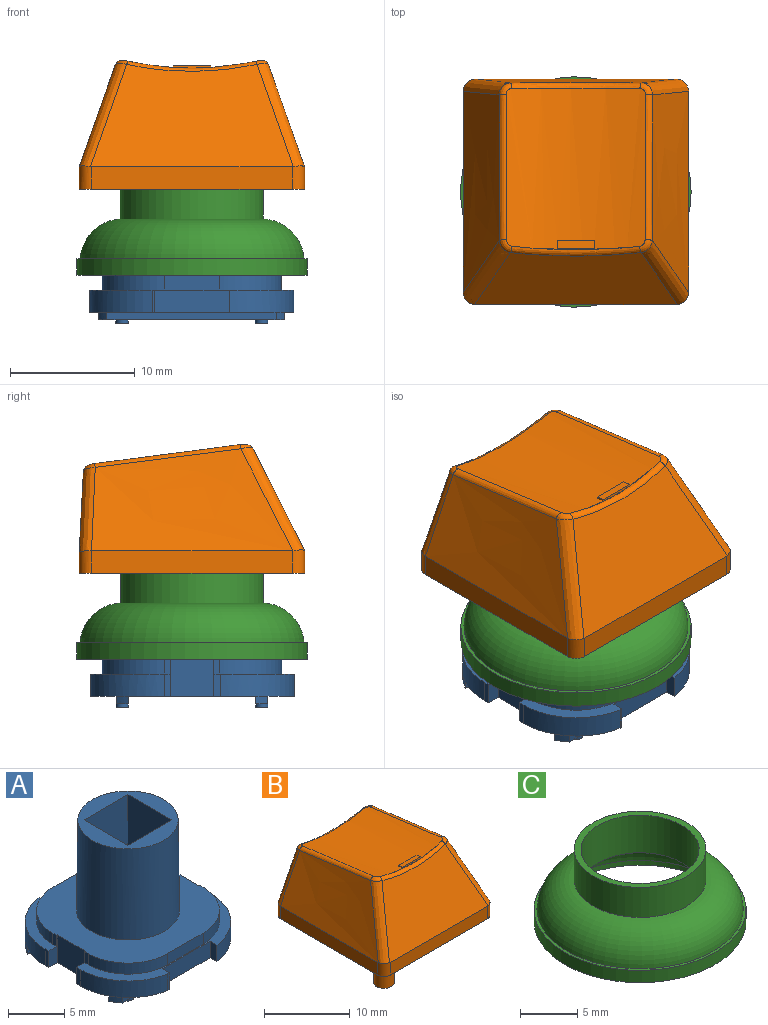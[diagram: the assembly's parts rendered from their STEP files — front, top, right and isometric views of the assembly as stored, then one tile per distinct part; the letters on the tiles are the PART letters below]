
ASSEMBLY  parts=3 mates=2
PART A: 86 faces, bbox 16.4x16.4x13.7 mm
  f0: plane 6x1.8mm, normal (0,1,0), area 10.8mm2, adj f3,f10,f11,f12
  f1: plane 1x1mm, normal (0,0,-1), area 0.8mm2, adj f13
  f2: plane 1x1mm, normal (0,0,-1), area 0.8mm2, adj f14
  f3: plane 1.8x0.85mm, normal (1,0,0), area 1.5mm2, adj f0,f11,f12,f26
  f4: plane 1.2x0.45mm, normal (-1,0,0), area 0.5mm2, adj f5,f11,f27,f28
  f5: revolved ~5x5mm, area 9.4mm2, adj f4,f6,f11,f28
  f6: plane 4.4x1.2mm, normal (0,1,0), area 5.3mm2, adj f5,f7,f11,f28
  f7: revolved ~5x5mm, area 9.4mm2, adj f6,f9,f11,f28
  f8: revolved ~9.8x9.13mm, area 277.6mm2, adj f19,f28
  f9: plane 1.2x0.45mm, normal (1,0,0), area 0.5mm2, adj f7,f11,f28,f29
  f10: plane 1.8x0.85mm, normal (-1,0,0), area 1.5mm2, adj f0,f11,f12,f31
  f11: plane 16.4x6.4mm, normal (0,0,1), area 17.2mm2, adj f0,f3,f4,f5,f6,f7,f9,f10
  f12: plane 13.52x2.05mm, normal (0,0,-1), area 17.2mm2, adj f0,f3,f10,f15,f26,f31
  f13: revolved ~1x1mm, area 0.9mm2, adj f1,f32,f33
  f14: revolved ~1x1mm, area 0.9mm2, adj f2,f33,f34
  f15: plane 13.52x0.6mm, normal (0,1,0), area 8.1mm2, adj f12,f32,f33,f34,f35,f36
  f16: plane 2.8x0.75mm, normal (0,0,-1), area 2.1mm2, adj f40,f41,f42,f43
  f17: plane 2.8x0.75mm, normal (0,0,-1), area 2.1mm2, adj f44,f45,f46,f47
  f18: plane 2.8x0.75mm, normal (0,0,-1), area 2.1mm2, adj f48,f49,f50,f51
  f19: plane 8.9x8.9mm, normal (0,0,1), area 32mm2, adj f8,f43,f47,f51,f52
  f20: plane 2.8x0.75mm, normal (0,0,-1), area 2.1mm2, adj f37,f38,f39,f52
  f21: revolved ~5x5mm, area 9.4mm2, adj f22,f24,f28,f55
  f22: plane 4.4x1.2mm, normal (0,-1,0), area 5.3mm2, adj f21,f23,f28,f55
  f23: revolved ~5x5mm, area 9.4mm2, adj f22,f28,f53,f55
  f24: plane 1.2x0.45mm, normal (1,0,0), area 0.5mm2, adj f21,f28,f55,f57
  f25: plane 1.8x0.45mm, normal (-1,0,0), area 0.8mm2, adj f11,f26,f27,f58
  f26: revolved ~5.95x5.2mm, area 15.5mm2, adj f3,f11,f12,f25,f35,f58
  f27: plane 3x1.1mm, normal (0,-1,0), area 2.1mm2, adj f4,f11,f25,f28,f58,f59,f72
  f28: plane 14.4x14.4mm, normal (0,0,1), area 119.7mm2, adj f4,f5,f6,f7,f8,f9,f21,f22
  f29: plane 3x1.1mm, normal (0,-1,0), area 2.1mm2, adj f9,f11,f28,f30,f60,f61,f72
  f30: plane 1.8x0.45mm, normal (1,0,0), area 0.8mm2, adj f11,f29,f31,f61
  f31: revolved ~5.95x5.2mm, area 15.5mm2, adj f10,f11,f12,f30,f36,f61
  f32: plane 1.86x1mm, normal (0,0,-1), area 1.1mm2, adj f13,f15,f36,f62
  f33: plane 11.2x1mm, normal (0,0,-1), area 10.4mm2, adj f13,f14,f15,f62
  f34: plane 1.85x1mm, normal (0,0,-1), area 1.1mm2, adj f14,f15,f35,f62
  f35: revolved ~1x0.69mm, area 0.7mm2, adj f15,f26,f34,f62
  f36: revolved ~1x0.69mm, area 0.7mm2, adj f15,f31,f32,f62
  f37: plane 5.9x0.75mm, normal (0,1,0), area 4.4mm2, adj f20,f38,f52,f63
  f38: plane 5.9x2.8mm, normal (1,0,0), area 16.5mm2, adj f20,f37,f39,f63
  f39: plane 5.9x0.75mm, normal (0,-1,0), area 4.4mm2, adj f20,f38,f52,f63
  f40: plane 5.9x0.75mm, normal (1,0,0), area 4.4mm2, adj f16,f41,f43,f63
  f41: plane 5.9x2.8mm, normal (0,-1,0), area 16.5mm2, adj f16,f40,f42,f63
  f42: plane 5.9x0.75mm, normal (-1,0,0), area 4.4mm2, adj f16,f41,f43,f63
  f43: plane 12.8x5.5mm, normal (0,-1,0), area 53.9mm2, adj f16,f19,f40,f42,f47,f52,f63
  f44: plane 5.9x0.75mm, normal (0,-1,0), area 4.4mm2, adj f17,f45,f47,f63
  f45: plane 5.9x2.8mm, normal (-1,0,0), area 16.5mm2, adj f17,f44,f46,f63
  f46: plane 5.9x0.75mm, normal (0,1,0), area 4.4mm2, adj f17,f45,f47,f63
  f47: plane 12.8x5.5mm, normal (-1,0,0), area 53.9mm2, adj f17,f19,f43,f44,f46,f51,f63
  f48: plane 5.9x0.75mm, normal (-1,0,0), area 4.4mm2, adj f18,f49,f51,f63
  f49: plane 5.9x2.8mm, normal (0,1,0), area 16.5mm2, adj f18,f48,f50,f63
  f50: plane 5.9x0.75mm, normal (1,0,0), area 4.4mm2, adj f18,f49,f51,f63
  f51: plane 12.8x5.5mm, normal (0,1,0), area 53.9mm2, adj f18,f19,f47,f48,f50,f52,f63
  f52: plane 12.8x5.5mm, normal (1,0,0), area 53.9mm2, adj f19,f20,f37,f39,f43,f51,f63
  f53: plane 1.2x0.45mm, normal (-1,0,0), area 0.5mm2, adj f23,f28,f55,f64
  f54: plane 1.8x0.2mm, normal (0,-1,0), area 0.4mm2, adj f55,f66,f70,f77
  f55: plane 16.4x6.45mm, normal (0,0,1), area 17.6mm2, adj f21,f22,f23,f24,f53,f54,f56,f57
  f56: plane 1.8x0.45mm, normal (1,0,0), area 0.8mm2, adj f55,f57,f69,f71
  f57: plane 3x1.1mm, normal (0,1,0), area 2.1mm2, adj f24,f28,f55,f56,f60,f71,f72
  f58: plane 3.35x1.93mm, normal (0,0,-1), area 3.5mm2, adj f25,f26,f27,f62,f72
  f59: plane 3.5x3mm, normal (-1,0,0), area 10.5mm2, adj f27,f28,f64,f72
  f60: plane 3.5x3mm, normal (1,0,0), area 10.5mm2, adj f28,f29,f57,f72
  f61: plane 3.35x1.93mm, normal (0,0,-1), area 3.5mm2, adj f29,f30,f31,f62,f72
  f62: plane 14.91x0.6mm, normal (0,-1,0), area 8.9mm2, adj f32,f33,f34,f35,f36,f58,f61,f72
  f63: plane 9.2x9.2mm, normal (0,0,-1), area 27.8mm2, adj f37,f38,f39,f40,f41,f42,f43,f44
  f64: plane 3x1.1mm, normal (0,1,0), area 2.1mm2, adj f28,f53,f55,f59,f65,f72,f73
  f65: plane 1.8x0.53mm, normal (-1,0,0), area 1mm2, adj f55,f64,f70,f73
  f66: plane 1.8x0.9mm, normal (1,0,0), area 1.6mm2, adj f54,f55,f67,f77
  f67: plane 6x1.8mm, normal (0,-1,0), area 10.8mm2, adj f55,f66,f68,f77
  f68: plane 1.8x0.85mm, normal (-1,0,0), area 1.5mm2, adj f55,f67,f69,f77
  f69: revolved ~5.95x5.2mm, area 15.5mm2, adj f55,f56,f68,f71,f75,f77
  f70: revolved ~5.92x5mm, area 15.2mm2, adj f54,f55,f65,f73,f77,f78
  f71: plane 3.35x1.93mm, normal (0,0,-1), area 3.5mm2, adj f56,f57,f69,f72,f79
  f72: plane 14.4x10.2mm, normal (0,0,-1), area 76.3mm2, adj f27,f29,f57,f58,f59,f60,f61,f62
  f73: plane 3.35x1.93mm, normal (0,0,-1), area 3.6mm2, adj f64,f65,f70,f72,f79
  f74: plane 1x1mm, normal (0,0,-1), area 0.8mm2, adj f80
  f75: revolved ~1x0.69mm, area 0.7mm2, adj f69,f76,f79,f81
  f76: plane 1.86x1mm, normal (0,0,-1), area 1.1mm2, adj f75,f79,f80,f81
  f77: plane 13.59x2.1mm, normal (0,0,-1), area 17.5mm2, adj f54,f66,f67,f68,f69,f70,f81
  f78: revolved ~1x0.67mm, area 0.7mm2, adj f70,f79,f81,f82
  f79: plane 14.95x0.6mm, normal (0,1,0), area 9mm2, adj f71,f72,f73,f75,f76,f78,f82,f83
  f80: revolved ~1x1mm, area 0.9mm2, adj f74,f76,f83
  f81: plane 13.59x0.6mm, normal (0,-1,0), area 8.2mm2, adj f75,f76,f77,f78,f82,f83
  f82: plane 1.9x1mm, normal (0,0,-1), area 1.2mm2, adj f78,f79,f81,f84
  f83: plane 11.2x1mm, normal (0,0,-1), area 10.4mm2, adj f79,f80,f81,f84
  f84: revolved ~1x1mm, area 0.9mm2, adj f82,f83,f85
  f85: plane 1x1mm, normal (0,0,-1), area 0.8mm2, adj f84
PART B: 47 faces, bbox 21.1x23x22.5 mm
  f0: cylinder r=22.9mm len=12.92mm, axis (0,0.99,-0.13), area 141.3mm2, adj f18,f19,f20,f21,f22,f23,f24,f25
  f1: plane 18.1x18.1mm, normal (0,0,-1), area 67.5mm2, adj f2,f3,f4,f5,f10,f12,f14,f16
  f2: plane 16.1x1.8mm, normal (1,0,0), area 29mm2, adj f1,f9,f10,f16
  f3: plane 16.11x1.81mm, normal (0,1,0), area 29mm2, adj f1,f6,f14,f15,f16,f17
  f4: plane 16.1x1.8mm, normal (-1,0,0), area 29mm2, adj f1,f7,f12,f14
  f5: plane 16.1x1.8mm, normal (0,-1,0), area 29mm2, adj f1,f8,f10,f12
  f6: plane 15.97x6.36mm, normal (0,1,0.05), area 80mm2, adj f3,f15,f17,f20
  f7: bspline ~18.1x8.73mm, area 112.7mm2, adj f4,f12,f13,f14,f15,f19
  f8: plane 16.3x8.23mm, normal (0,-0.89,0.45), area 118.9mm2, adj f5,f10,f11,f12,f13,f23
  f9: bspline ~18.1x8.73mm, area 112.7mm2, adj f2,f10,f11,f16,f17,f24
  f10: cylinder r=1mm len=1.87mm, axis (0,0,-1), area 2.9mm2, adj f1,f2,f5,f8,f9,f11
  f11: bspline ~10.61x6.11mm, area 13.9mm2, adj f8,f9,f10,f25
  f12: cylinder r=1mm len=1.87mm, axis (0,0,1), area 2.9mm2, adj f1,f4,f5,f7,f8,f13
  f13: bspline ~10.63x6.12mm, area 13.9mm2, adj f7,f8,f12,f21
  f14: cylinder r=1mm len=1.81mm, axis (0,0,-1), area 2.8mm2, adj f1,f3,f4,f7,f15
  f15: bspline ~8.47x4.4mm, area 11mm2, adj f3,f6,f7,f14,f18
  f16: cylinder r=1mm len=1.81mm, axis (0,0,1), area 2.8mm2, adj f1,f2,f3,f9,f17
  f17: bspline ~8.46x4.39mm, area 11mm2, adj f3,f6,f9,f16,f22
  f18: bspline ~1.18x1.07mm, area 0.8mm2, adj f0,f15,f19,f20
  f19: bspline ~18.54x2.8mm, area 8.6mm2, adj f0,f7,f18,f21
  f20: bspline ~10.51x1.06mm, area 7.3mm2, adj f0,f6,f18,f22
  f21: bspline ~1.18x1.11mm, area 0.8mm2, adj f0,f13,f19,f23
  f22: bspline ~1.22x1.01mm, area 0.8mm2, adj f0,f17,f20,f24
  f23: bspline ~10.48x0.82mm, area 6.5mm2, adj f0,f8,f21,f25
  f24: bspline ~18.54x2.8mm, area 8.6mm2, adj f0,f9,f22,f25
  f25: bspline ~1.28x1.05mm, area 0.8mm2, adj f0,f11,f23,f24
  f26: plane 16.12x1.65mm, normal (-1,0,0), area 26mm2, adj f1,f27,f29,f32,f33
  f27: plane 16.1x1.77mm, normal (0,-1,0), area 28.6mm2, adj f1,f26,f28,f30,f31,f33
  f28: plane 16.12x1.65mm, normal (1,0,0), area 26mm2, adj f1,f27,f29,f31,f32
  f29: plane 16.1x1.56mm, normal (0,1,0), area 25.1mm2, adj f1,f26,f28,f32
  f30: plane 16.17x6.17mm, normal (0,-1,-0.05), area 75.1mm2, adj f27,f31,f33,f34
  f31: offset ~20.1x10.73mm, area 104.4mm2, adj f27,f28,f30,f32,f34
  f32: plane 16.52x8.13mm, normal (0,0.89,-0.45), area 111.3mm2, adj f26,f28,f29,f31,f33,f34
  f33: offset ~20.1x10.73mm, area 104.4mm2, adj f26,f27,f30,f32,f34
  f34: cylinder r=23.9mm len=11.98mm, axis (0,0.99,-0.13), area 102mm2, adj f30,f31,f32,f33,f36,f37,f38,f39
  f35: plane 5.3x5.3mm, normal (0,0,-1), area 23.6mm2, adj f36,f37,f38,f39,f45
  f36: plane 14.05x5.34mm, normal (0,1,0), area 73.7mm2, adj f34,f35,f37,f38
  f37: plane 14.7x5.3mm, normal (1,0,0), area 76.1mm2, adj f34,f35,f36,f39
  f38: plane 14.7x5.3mm, normal (-1,0,0), area 76.1mm2, adj f34,f35,f36,f39
  f39: plane 14.74x5.34mm, normal (0,-1,0), area 77.4mm2, adj f34,f35,f37,f38
  f40: plane 0.71x0.24mm, normal (1,0,0), area 0.1mm2, adj f0,f41,f43,f44
  f41: plane 3x0.2mm, normal (0,0.99,-0.13), area 0.6mm2, adj f0,f40,f42,f44
  f42: plane 0.71x0.24mm, normal (-1,0,0), area 0.1mm2, adj f0,f41,f43,f44
  f43: plane 3x0.2mm, normal (0,-0.99,0.13), area 0.6mm2, adj f0,f40,f42,f44
  f44: plane 3x0.69mm, normal (0,0.13,0.99), area 2.1mm2, adj f40,f41,f42,f43
  f45: cylinder r=1.2mm len=3.5mm, axis (0,0,1), area 26.4mm2, adj f35,f46
  f46: plane 2.4x2.4mm, normal (0,0,-1), area 4.5mm2, adj f45
PART C: 9 faces, bbox 19.5x19.5x7.7 mm
  f0: cylinder r=9.25mm len=18.5mm, axis (0,0,1), area 76.2mm2, adj f1,f8
  f1: plane 18.5x18.5mm, normal (0,0,-1), area 41.8mm2, adj f0,f2
  f2: cylinder r=8.5mm len=17mm, axis (0,0,1), area 27.5mm2, adj f1,f3
  f3: torus R=5.16mm, axis (0,0,1), area 232.3mm2, adj f2,f4
  f4: cylinder r=5.15mm len=10.3mm, axis (0,0,1), area 129.4mm2, adj f3,f5
  f5: plane 11.5x11.5mm, normal (0,0,1), area 20.5mm2, adj f4,f6
  f6: cylinder r=5.75mm len=11.5mm, axis (0,0,1), area 115.6mm2, adj f5,f7
  f7: torus R=5.6mm, axis (0,0,1), area 243.6mm2, adj f6,f8
  f8: plane 18.5x18.5mm, normal (0,0,1), area 14.3mm2, adj f0,f7
PLACE A at identity fixed
PLACE B t=(0,0,9.9)mm
PLACE C t=(0,0,3)mm
MATE fastened A.f28 <-> C.f0  axis (0,0,1) through (0,0,3)mm
MATE fastened A.f19 <-> B.f45  axis (0,0,1) through (0,0,12.8)mm
